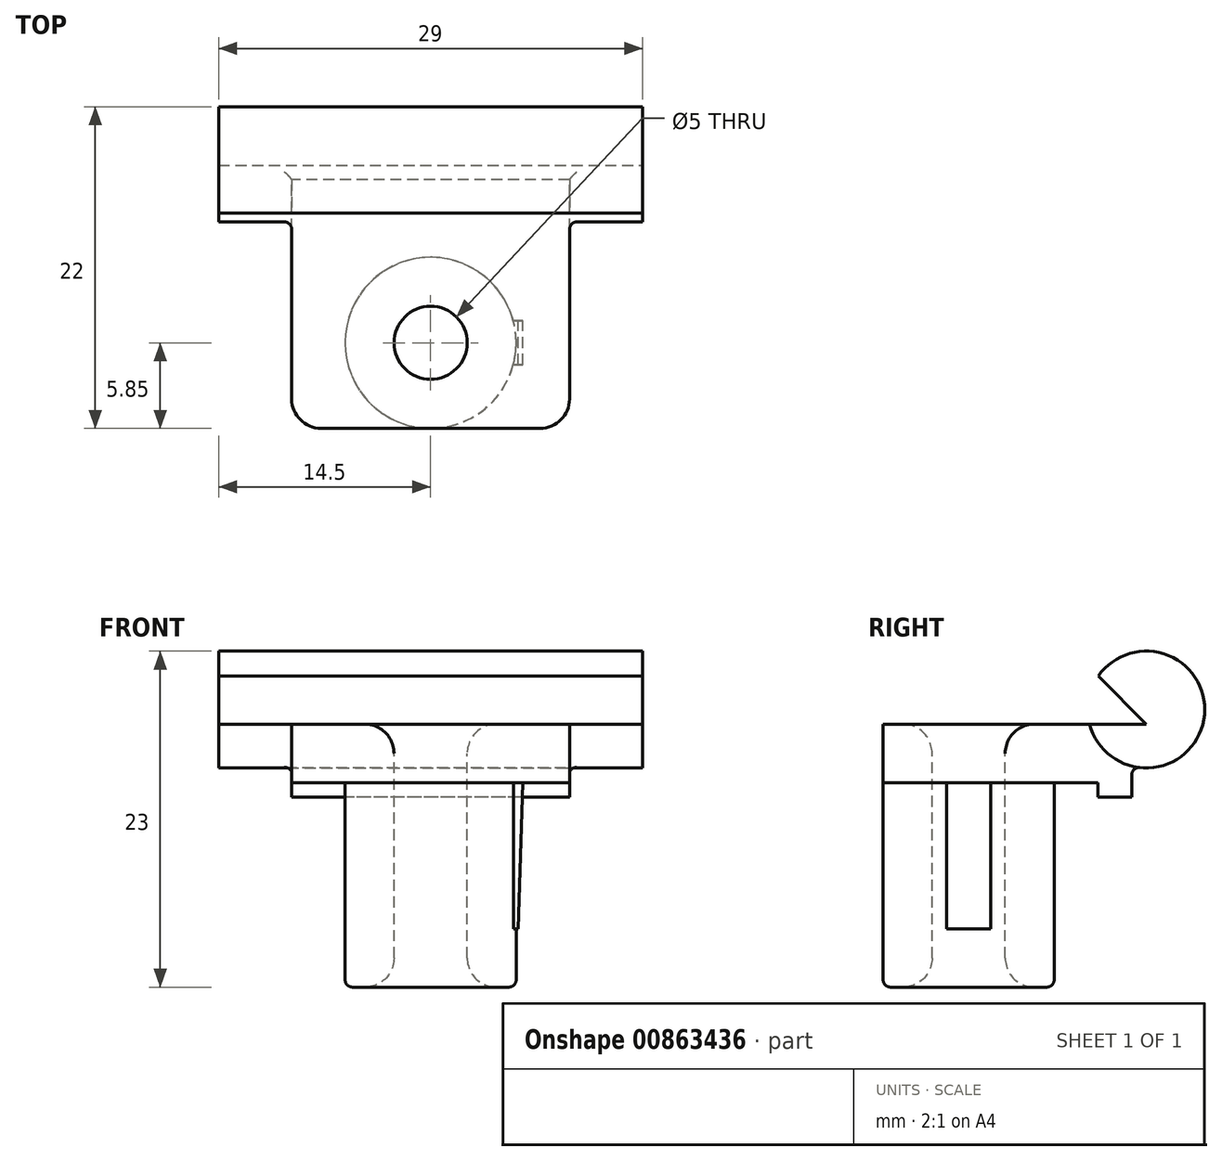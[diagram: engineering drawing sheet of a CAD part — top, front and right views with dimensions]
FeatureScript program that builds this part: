
annotation { "Feature Type Name" : "Feature", "Feature Type Description" : "" }
export const myFeature = defineFeature(function(context is Context, id is Id, definition is map)
    precondition{}
    {
        {
            var Q0;
            Q0=qCreatedBy(makeId("Top.planeOp"),FACE);
            var sketch = newSketch(context, id + "F0", { "sketchPlane" : qUnion([Q0])});
            skCircle(sketch, "E0", {"center": v(0, 0) * mm, "radius": 5.85 * mm});
            skSolve(sketch);
        }
        {
            var Q0;
            Q0 = qSketchRegion(id + "F0", true);
            extrude(context, id + "F1", {"entities" : qUnion([Q0]), "oppositeDirection" : true, "depth" : 14 * mm, "offsetDistance" : 25 * mm});
        }
        {
            var Q0;
            Q0=qCreatedBy(makeId("Top.planeOp"),FACE);
            var sketch = newSketch(context, id + "F2", { "sketchPlane" : qUnion([Q0])});
            skLineSegment(sketch, "E1.bottom", {"start": v(-9.5, 11.15) * mm, "end": v(9.5, 11.15) * mm});
            skLineSegment(sketch, "E1.top", {"start": v(-9.5, -5.85) * mm, "end": v(9.5, -5.85) * mm});
            skLineSegment(sketch, "E1.left", {"start": v(-9.5, 11.15) * mm, "end": v(-9.5, -5.85) * mm});
            skLineSegment(sketch, "E1.right", {"start": v(9.5, 11.15) * mm, "end": v(9.5, -5.85) * mm});
            skPoint(sketch, "E2", {"position": v(0, -5.85) * mm});
            skSolve(sketch);
        }
        {
            var Q0;
            Q0 = qSketchRegion(id + "F2", true);
            extrude(context, id + "F3", {"entities" : qUnion([Q0]), "operationType" : NewBodyOperationType.ADD, "depth" : 4 * mm, "offsetDistance" : 25 * mm});
        }
        {
            var Q0;
            Q0=qCreatedBy(makeId("Top.planeOp"),FACE);
            var sketch = newSketch(context, id + "F4", { "sketchPlane" : qUnion([Q0])});
            skPoint(sketch, "E3.0", {"position": v(9.5, 11.15) * mm});
            skPoint(sketch, "E4.0", {"position": v(-9.5, 11.15) * mm});
            skLineSegment(sketch, "E5.bottom", {"start": v(9.5, 11.15) * mm, "end": v(-9.5, 11.15) * mm});
            skLineSegment(sketch, "E5.top", {"start": v(9.5, 8.85) * mm, "end": v(-9.5, 8.85) * mm});
            skLineSegment(sketch, "E5.left", {"start": v(9.5, 11.15) * mm, "end": v(9.5, 8.85) * mm});
            skLineSegment(sketch, "E5.right", {"start": v(-9.5, 11.15) * mm, "end": v(-9.5, 8.85) * mm});
            skSolve(sketch);
        }
        {
            var Q0;
            Q0 = qSketchRegion(id + "F4", true);
            extrude(context, id + "F5", {"entities" : qUnion([Q0]), "operationType" : NewBodyOperationType.ADD, "oppositeDirection" : true, "depth" : 1 * mm, "offsetDistance" : 25 * mm});
        }
        {
            var Q0;
            Q0=qCreatedBy(makeId("Front.planeOp"),FACE);
            var sketch = newSketch(context, id + "F6", { "sketchPlane" : qUnion([Q0])});
            skLineSegment(sketch, "E6", {"start": v(6.3, 0) * mm, "end": v(6, -10) * mm});
            skLineSegment(sketch, "E7", {"start": v(6, -10) * mm, "end": v(5, -10) * mm});
            skLineSegment(sketch, "E8", {"start": v(5, -10) * mm, "end": v(5, 0) * mm});
            skLineSegment(sketch, "E9", {"start": v(5, 0) * mm, "end": v(6.3, 0) * mm});
            skLineSegment(sketch, "E10", {"start": v(0, 0) * mm, "end": v(0, -18.9) * mm, "construction": true});
            skSolve(sketch);
        }
        {
            var Q0;
            Q0 = qSketchRegion(id + "F6", true);
            extrude(context, id + "F7", {"entities" : qUnion([Q0]), "operationType" : NewBodyOperationType.ADD, "endBound" : BoundingType.SYMMETRIC, "depth" : 3 * mm, "offsetDistance" : 25 * mm});
        }
        {
            var Q0;
            Q0=qCreatedBy(makeId("Right.planeOp"),FACE);
            var sketch = newSketch(context, id + "F8", { "sketchPlane" : qUnion([Q0])});
            skArc(sketch, "E11", {"start": v(8.28, 4) * mm, "mid": v(16.09, 4.3) * mm, "end": v(8.87, 7.28) * mm});
            skLineSegment(sketch, "E12", {"start": v(8.28, 4) * mm, "end": v(12.15, 4) * mm});
            skLineSegment(sketch, "E13", {"start": v(12.15, 4) * mm, "end": v(8.87, 7.28) * mm});
            skPoint(sketch, "E14", {"position": v(12.15, 1) * mm});
            skPoint(sketch, "E15", {"position": v(16.15, 5) * mm});
            skSolve(sketch);
        }
        {
            var Q0;
            Q0 = qSketchRegion(id + "F8", true);
            extrude(context, id + "F9", {"entities" : qUnion([Q0]), "operationType" : NewBodyOperationType.ADD, "endBound" : BoundingType.SYMMETRIC, "oppositeDirection" : true, "depth" : 29 * mm, "offsetDistance" : 25 * mm});
        }
        {
            var Q0;
            Q0=qCreatedBy(makeId("Top.planeOp"),FACE);
            var sketch = newSketch(context, id + "F10", { "sketchPlane" : qUnion([Q0])});
            skCircle(sketch, "E16", {"center": v(0, 0) * mm, "radius": 2.5 * mm});
            skSolve(sketch);
        }
        {
            var Q0;
            Q0 = qSketchRegion(id + "F10", true);
            extrude(context, id + "F11", {"entities" : qUnion([Q0]), "operationType" : NewBodyOperationType.REMOVE, "endBound" : BoundingType.SYMMETRIC, "oppositeDirection" : true, "depth" : 30 * mm, "offsetDistance" : 25 * mm});
        }
        {
            var Q0;
            Q0=makeQuery(id+"F3.opExtrude","SWEPT_EDGE",EDGE,{"disambiguationData":[OSD([sQuery(id+"F2.wireOp",EDGE,"E1.top"),sQuery(id+"F2.wireOp",EDGE,"E1.left")])]});
            var Q1;
            Q1=makeQuery(id+"F3.opExtrude","SWEPT_EDGE",EDGE,{"disambiguationData":[OSD([sQuery(id+"F2.wireOp",EDGE,"E1.top"),sQuery(id+"F2.wireOp",EDGE,"E1.right")])]});
            var Q2;
            Q2=makeQuery(id+"F11.boolean.opBoolean","INTERSECT",EDGE,{"derivedFrom":[makeQuery(id+"F1.opExtrude","CAP_FACE",FACE,{"disambiguationData":[OSD([sQuery(id+"F0.wireOp",EDGE,"E0")])],"isStart":false}),makeQuery(id+"F11.opExtrude","SWEPT_FACE",FACE,{"disambiguationData":[OSD([sQuery(id+"F10.wireOp",EDGE,"E16")])]})]});
            var Q3;
            Q3=makeQuery(id+"F11.boolean.opBoolean","INTERSECT",EDGE,{"derivedFrom":[makeQuery(id+"F9.boolean.opBoolean","MERGE",FACE,{"derivedFrom":[makeQuery(id+"F3.opExtrude","CAP_FACE",FACE,{"disambiguationData":[OSD([sQuery(id+"F2.wireOp",EDGE,"E1.bottom"),sQuery(id+"F2.wireOp",EDGE,"E1.top"),sQuery(id+"F2.wireOp",EDGE,"E1.left"),sQuery(id+"F2.wireOp",EDGE,"E1.right")])],"isStart":false}),makeQuery(id+"F9.opExtrude","SWEPT_FACE",FACE,{"disambiguationData":[OSD([sQuery(id+"F8.wireOp",EDGE,"E12")])]})]}),makeQuery(id+"F11.opExtrude","SWEPT_FACE",FACE,{"disambiguationData":[OSD([sQuery(id+"F10.wireOp",EDGE,"E16")])]})]});
            fillet(context, id + "F12", {"entities" : qUnion([Q0, Q1, Q2, Q3]), "radius" : 2 * mm, "tangentPropagation" : true, "allowEdgeOverflow" : false});
        }
        {
            var Q0;
            Q0=makeQuery(id+"F1.opExtrude","CAP_EDGE",EDGE,{"disambiguationData":[OSD([sQuery(id+"F0.wireOp",EDGE,"E0")])],"isStart":false});
            var Q1;
            Q1=makeQuery(id+"F5.opExtrude","CAP_EDGE",EDGE,{"disambiguationData":[OSD([sQuery(id+"F4.wireOp",EDGE,"E5.top")])],"isStart":true});
            var Q2;
            {var subQ0=sQuery(id+"F0.wireOp",EDGE,"E0");Q2=makeQuery(id+"F7.boolean.opBoolean","SPLIT",EDGE,{"disambiguationData":[TD([makeQuery(id+"F7.opExtrude","CAP_FACE",FACE,{"disambiguationData":[OSD([sQuery(id+"F6.wireOp",EDGE,"E6"),sQuery(id+"F6.wireOp",EDGE,"E7"),sQuery(id+"F6.wireOp",EDGE,"E8"),sQuery(id+"F6.wireOp",EDGE,"E9")])],"isStart":false})])],"derivedFrom":makeQuery(id+"F1.opExtrude","CAP_EDGE",EDGE,{"disambiguationData":[OSD([subQ0])],"isStart":true})});}
            var Q3;
            {var subQ0=sQuery(id+"F0.wireOp",EDGE,"E0");var subQ4=sQuery(id+"F6.wireOp",EDGE,"E9");var subQ5=sQuery(id+"F6.wireOp",EDGE,"E8");var subQ6=sQuery(id+"F6.wireOp",EDGE,"E7");var subQ7=sQuery(id+"F6.wireOp",EDGE,"E6");var subQ8=makeQuery(id+"F7.opExtrude","CAP_FACE",FACE,{"disambiguationData":[OSD([subQ7,subQ6,subQ5,subQ4])],"isStart":true});Q3=makeQuery(id+"FBk2GZocxT7X6n4_1.3.F7.boolean.opBoolean","SPLIT",EDGE,{"disambiguationData":[TD([subQ8])],"derivedFrom":makeQuery(id+"FBk2GZocxT7X6n4_1.2.F7.boolean.opBoolean","SPLIT",EDGE,{"disambiguationData":[TD([subQ8])],"derivedFrom":makeQuery(id+"F7.boolean.opBoolean","SPLIT",EDGE,{"disambiguationData":[TD([subQ8])],"derivedFrom":makeQuery(id+"F1.opExtrude","CAP_EDGE",EDGE,{"disambiguationData":[OSD([subQ0])],"isStart":true})})})});}
            var Q4;
            {var subQ0=sQuery(id+"F0.wireOp",EDGE,"E0");var subQ4=sQuery(id+"F6.wireOp",EDGE,"E9");var subQ5=sQuery(id+"F6.wireOp",EDGE,"E8");var subQ6=sQuery(id+"F6.wireOp",EDGE,"E7");var subQ7=sQuery(id+"F6.wireOp",EDGE,"E6");var subQ8=makeQuery(id+"FBk2GZocxT7X6n4_1.2.F7.opExtrude","CAP_FACE",FACE,{"disambiguationData":[OSD([subQ7,subQ6,subQ5,subQ4])],"isStart":false});var subQ9=makeQuery(id+"F7.opExtrude","CAP_FACE",FACE,{"disambiguationData":[OSD([subQ7,subQ6,subQ5,subQ4])],"isStart":true});Q4=makeQuery(id+"FBk2GZocxT7X6n4_1.3.F7.boolean.opBoolean","SPLIT",EDGE,{"disambiguationData":[TD([subQ8])],"derivedFrom":makeQuery(id+"FBk2GZocxT7X6n4_1.2.F7.boolean.opBoolean","SPLIT",EDGE,{"disambiguationData":[TD([subQ9])],"derivedFrom":makeQuery(id+"F7.boolean.opBoolean","SPLIT",EDGE,{"disambiguationData":[TD([subQ9])],"derivedFrom":makeQuery(id+"F1.opExtrude","CAP_EDGE",EDGE,{"disambiguationData":[OSD([subQ0])],"isStart":true})})})});}
            var Q5;
            {var subQ0=sQuery(id+"F0.wireOp",EDGE,"E0");var subQ2=sQuery(id+"F6.wireOp",EDGE,"E9");var subQ3=sQuery(id+"F6.wireOp",EDGE,"E8");var subQ4=sQuery(id+"F6.wireOp",EDGE,"E7");var subQ5=sQuery(id+"F6.wireOp",EDGE,"E6");Q5=makeQuery(id+"FBk2GZocxT7X6n4_1.2.F7.boolean.opBoolean","SPLIT",EDGE,{"disambiguationData":[TD([makeQuery(id+"FBk2GZocxT7X6n4_1.1.F7.opExtrude","CAP_FACE",FACE,{"disambiguationData":[OSD([subQ5,subQ4,subQ3,subQ2])],"isStart":false})])],"derivedFrom":makeQuery(id+"F7.boolean.opBoolean","SPLIT",EDGE,{"disambiguationData":[TD([makeQuery(id+"F7.opExtrude","CAP_FACE",FACE,{"disambiguationData":[OSD([subQ5,subQ4,subQ3,subQ2])],"isStart":true})])],"derivedFrom":makeQuery(id+"F1.opExtrude","CAP_EDGE",EDGE,{"disambiguationData":[OSD([subQ0])],"isStart":true})})});}
            var Q6;
            Q6=makeQuery(id+"F9.boolean.opBoolean","INTERSECT",EDGE,{"derivedFrom":[makeQuery(id+"F5.boolean.opBoolean","MERGE",FACE,{"derivedFrom":[makeQuery(id+"F3.opExtrude","SWEPT_FACE",FACE,{"disambiguationData":[OSD([sQuery(id+"F2.wireOp",EDGE,"E1.bottom")])]}),makeQuery(id+"F5.opExtrude","SWEPT_FACE",FACE,{"disambiguationData":[OSD([sQuery(id+"F4.wireOp",EDGE,"E5.bottom")])]})]}),makeQuery(id+"F9.opExtrude","SWEPT_FACE",FACE,{"disambiguationData":[OSD([sQuery(id+"F8.wireOp",EDGE,"E11")])]})]});
            var Q7;
            Q7=makeQuery(id+"F9.boolean.opBoolean","INTERSECT",EDGE,{"derivedFrom":[makeQuery(id+"F5.boolean.opBoolean","MERGE",FACE,{"derivedFrom":[makeQuery(id+"F3.opExtrude","SWEPT_FACE",FACE,{"disambiguationData":[OSD([sQuery(id+"F2.wireOp",EDGE,"E1.left")])]}),makeQuery(id+"F5.opExtrude","SWEPT_FACE",FACE,{"disambiguationData":[OSD([sQuery(id+"F4.wireOp",EDGE,"E5.right")])]})]}),makeQuery(id+"F9.opExtrude","SWEPT_FACE",FACE,{"disambiguationData":[OSD([sQuery(id+"F8.wireOp",EDGE,"E11")])]})]});
            var Q8;
            Q8=makeQuery(id+"F9.boolean.opBoolean","INTERSECT",EDGE,{"derivedFrom":[makeQuery(id+"F5.boolean.opBoolean","MERGE",FACE,{"derivedFrom":[makeQuery(id+"F3.opExtrude","SWEPT_FACE",FACE,{"disambiguationData":[OSD([sQuery(id+"F2.wireOp",EDGE,"E1.right")])]}),makeQuery(id+"F5.opExtrude","SWEPT_FACE",FACE,{"disambiguationData":[OSD([sQuery(id+"F4.wireOp",EDGE,"E5.left")])]})]}),makeQuery(id+"F9.opExtrude","SWEPT_FACE",FACE,{"disambiguationData":[OSD([sQuery(id+"F8.wireOp",EDGE,"E11")])]})]});
            fillet(context, id + "F13", {"entities" : qUnion([Q0, Q1, Q2, Q3, Q4, Q5, Q6, Q7, Q8]), "radius" : 0.5 * mm, "tangentPropagation" : true, "allowEdgeOverflow" : false});
        }
    });
